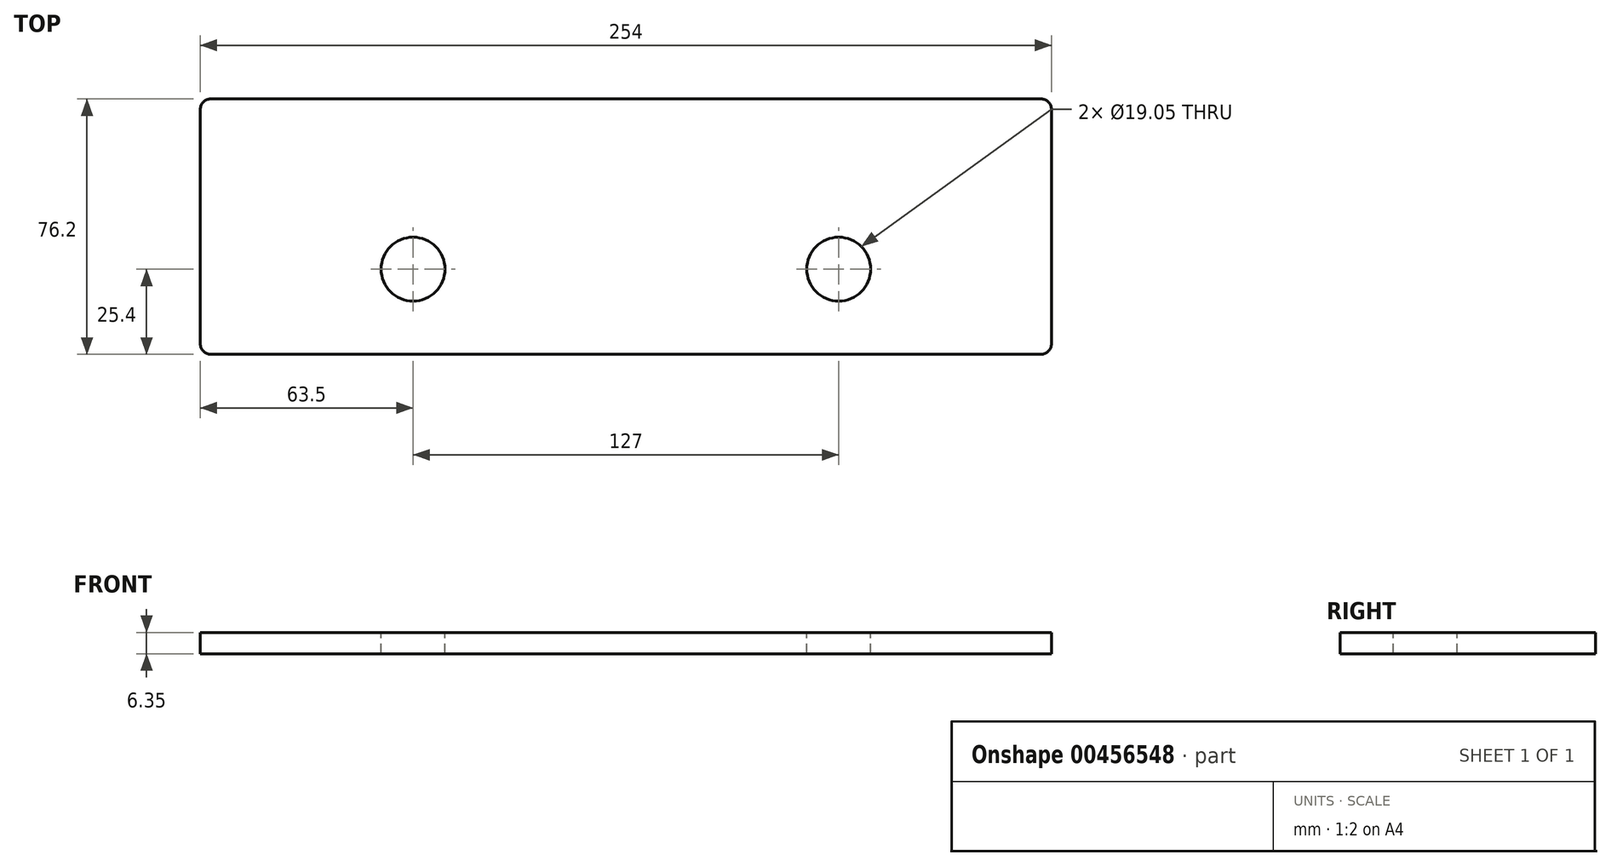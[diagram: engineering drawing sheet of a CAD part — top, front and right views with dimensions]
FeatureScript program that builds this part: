
annotation { "Feature Type Name" : "Feature", "Feature Type Description" : "" }
export const myFeature = defineFeature(function(context is Context, id is Id, definition is map)
    precondition{}
    {
        {
            var Q0;
            Q0=qCreatedBy(makeId("Top.planeOp"),FACE);
            var sketch = newSketch(context, id + "F0", { "sketchPlane" : qUnion([Q0])});
            skLineSegment(sketch, "E0", {"start": v(0, 0) * mm, "end": v(254, 0) * mm, "construction": true});
            skLineSegment(sketch, "E1", {"start": v(254, 0) * mm, "end": v(254, -76.2) * mm, "construction": true});
            skLineSegment(sketch, "E2.bottom", {"start": v(254, 0) * mm, "end": v(254, 0) * mm});
            skLineSegment(sketch, "E2.top", {"start": v(254, -76.2) * mm, "end": v(254, -76.2) * mm});
            skLineSegment(sketch, "E2.left", {"start": v(254, 0) * mm, "end": v(254, -76.2) * mm});
            skLineSegment(sketch, "E2.right", {"start": v(254, 0) * mm, "end": v(254, -76.2) * mm});
            skLineSegment(sketch, "E3.bottom", {"start": v(254, 0) * mm, "end": v(0, 0) * mm});
            skLineSegment(sketch, "E3.top", {"start": v(254, -76.2) * mm, "end": v(0, -76.2) * mm});
            skLineSegment(sketch, "E3.right", {"start": v(0, 0) * mm, "end": v(0, -76.2) * mm});
            skSolve(sketch);
        }
        {
            var Q0;
            Q0=makeQuery(id+"F0.imprint","IMPRINT",FACE,{"disambiguationData":[TD([[makeQuery(id+"F0.imprint","IMPRINT",EDGE,{"derivedFrom":sQuery(id+"F0.wireOp",EDGE,"E3.bottom")}),1.0]])]});
            extrude(context, id + "F1", {"entities" : qUnion([Q0]), "oppositeDirection" : true, "depth" : 6.35 * mm});
        }
        {
            var Q0;
            Q0=makeQuery(id+"F1.opExtrude","CAP_FACE",FACE,{"disambiguationData":[OSD([sQuery(id+"F0.wireOp",EDGE,"E3.bottom"),sQuery(id+"F0.wireOp",EDGE,"E3.top"),sQuery(id+"F0.wireOp",EDGE,"E2.left"),sQuery(id+"F0.wireOp",EDGE,"E3.right")])],"isStart":true});
            var sketch = newSketch(context, id + "F2", { "sketchPlane" : qUnion([Q0])});
            skLineSegment(sketch, "E4", {"start": v(0, -76.2) * mm, "end": v(127, -76.2) * mm, "construction": true});
            skLineSegment(sketch, "E5", {"start": v(127, -76.2) * mm, "end": v(127, -50.8) * mm, "construction": true});
            skLineSegment(sketch, "E6", {"start": v(127, -50.8) * mm, "end": v(63.5, -50.8) * mm, "construction": true});
            skLineSegment(sketch, "E7", {"start": v(63.5, -50.8) * mm, "end": v(190.5, -50.8) * mm, "construction": true});
            skCircle(sketch, "E8", {"center": v(63.5, -50.8) * mm, "radius": 9.53 * mm});
            skCircle(sketch, "E9", {"center": v(190.5, -50.8) * mm, "radius": 9.53 * mm});
            skSolve(sketch);
        }
        {
            var Q0;
            Q0=makeQuery(id+"F2.imprint","IMPRINT",FACE,{"disambiguationData":[TD([[makeQuery(id+"F2.imprint","IMPRINT",EDGE,{"derivedFrom":sQuery(id+"F2.wireOp",EDGE,"E8")}),1.0]])]});
            var Q1;
            Q1=makeQuery(id+"F2.imprint","IMPRINT",FACE,{"disambiguationData":[TD([[makeQuery(id+"F2.imprint","IMPRINT",EDGE,{"derivedFrom":sQuery(id+"F2.wireOp",EDGE,"E9")}),1.0]])]});
            extrude(context, id + "F3", {"entities" : qUnion([Q0, Q1]), "operationType" : NewBodyOperationType.REMOVE, "oppositeDirection" : true, "depth" : 25.4 * mm});
        }
        {
            var Q0;
            Q0=makeQuery(id+"F1.opExtrude","SWEPT_EDGE",EDGE,{"disambiguationData":[OSD([sQuery(id+"F0.wireOp",EDGE,"E3.top"),sQuery(id+"F0.wireOp",EDGE,"E2.left")])]});
            var Q1;
            Q1=makeQuery(id+"F1.opExtrude","SWEPT_EDGE",EDGE,{"disambiguationData":[OSD([sQuery(id+"F0.wireOp",EDGE,"E3.bottom"),sQuery(id+"F0.wireOp",EDGE,"E2.left")])]});
            var Q2;
            Q2=makeQuery(id+"F1.opExtrude","SWEPT_EDGE",EDGE,{"disambiguationData":[OSD([sQuery(id+"F0.wireOp",EDGE,"E3.top"),sQuery(id+"F0.wireOp",EDGE,"E3.right")])]});
            var Q3;
            Q3=makeQuery(id+"F1.opExtrude","SWEPT_EDGE",EDGE,{"disambiguationData":[OSD([sQuery(id+"F0.wireOp",EDGE,"E3.bottom"),sQuery(id+"F0.wireOp",EDGE,"E3.right")])]});
            fillet(context, id + "F4", {"entities" : qUnion([Q0, Q1, Q2, Q3]), "radius" : 3.17 * mm, "tangentPropagation" : true, "allowEdgeOverflow" : false});
        }
    });
